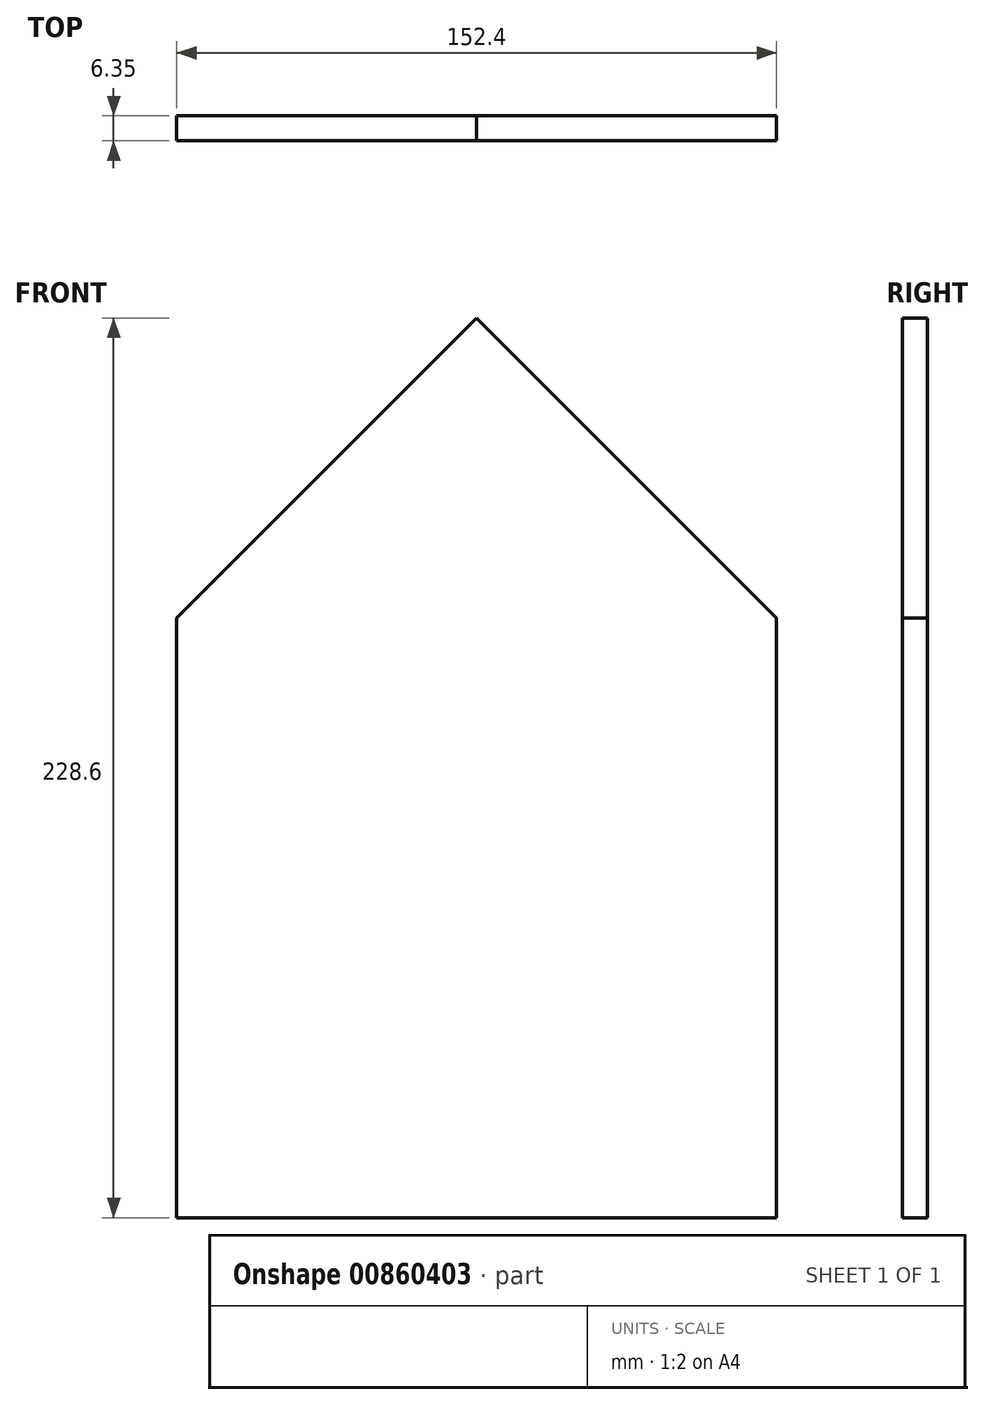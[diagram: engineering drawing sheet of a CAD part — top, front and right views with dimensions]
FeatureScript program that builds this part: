
annotation { "Feature Type Name" : "Feature", "Feature Type Description" : "" }
export const myFeature = defineFeature(function(context is Context, id is Id, definition is map)
    precondition{}
    {
        {
            var Q0;
            Q0=qCreatedBy(makeId("Front.planeOp"),FACE);
            var sketch = newSketch(context, id + "F0", { "sketchPlane" : qUnion([Q0])});
            skLineSegment(sketch, "E0.bottom", {"start": v(0, 0) * mm, "end": v(152.4, 0) * mm});
            skLineSegment(sketch, "E0.left", {"start": v(0, 0) * mm, "end": v(0, 152.4) * mm});
            skLineSegment(sketch, "E0.right", {"start": v(152.4, 0) * mm, "end": v(152.4, 152.4) * mm});
            skLineSegment(sketch, "E1", {"start": v(76.2, 228.6) * mm, "end": v(152.4, 152.4) * mm});
            skLineSegment(sketch, "E2", {"start": v(76.2, 228.6) * mm, "end": v(0, 152.4) * mm});
            skPoint(sketch, "E3.start.orphan", {"position": v(76.2, 0) * mm});
            skSolve(sketch);
        }
        {
            var Q0;
            Q0 = qSketchRegion(id + "F0", true);
            extrude(context, id + "F1", {"entities" : qUnion([Q0]), "depth" : 6.35 * mm, "offsetDistance" : 25.4 * mm});
        }
    });
